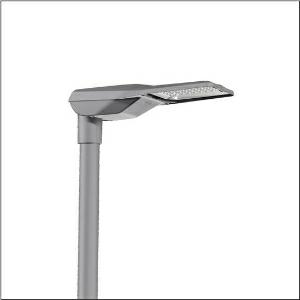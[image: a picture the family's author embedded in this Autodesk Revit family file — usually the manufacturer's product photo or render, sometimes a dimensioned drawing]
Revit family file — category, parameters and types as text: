
# Revit family: streetlight_sl_21_iq_mini___st0_8a_5xe2c31d08hb_f94e
name_source: partatom
category: Lighting Fixtures
units: mm (PartAtom-declared; Revit-internal decimal feet)

## family parameters
Cut with Voids When Loaded = No
Host = Face
Light Source = No
Part Type = Normal
Room Calculation Point = No
Round Connector Dimension = Use Diameter
Shared = No

## types (1)
- --- (1 x LED, 9450 lm, 70.9 W, 3000K)
    Apparent Load = 71 VA
    CIE Flux Codes = 38 75 97 100 100
    Color Rendering = 70
    Color Temperature = 3000K
    Default Elevation = 1800 mm
    Description = Streetlight SL 21 iQ mini, mast luminaire, primary light control with lens, of PMMA, primary optical cover: cover, of toughened safety glass, transparent, light distribution: ST0.8a, light emission: direct distribution, primary light characteristic: asymmetric, installation type: post-top, side-entry, LED, High Power LED, rated luminous flux: 9.450lm, luminous efficacy: 133lm/W, light colour: 730, colour temperature: 3000K, control gear: iQ-Comfort, control: Auto-Match, Temp-Guard, Lumen-Switch, Night-Set, Smart-Wire, Light-Fading, Desk-Remote (wireless, voltage-free reading and setting of iQ features in the workshop via application-optimized NFC function/RFID function), optimised constant luminous flux control (CLO 2.0), pre-setting: linear dimming characteristic, mains connection: 220..240V, AC, 50/60Hz, start of lifetime: 71W, end of service life: 75W, reduction: 31W, luminaire housing, of diecast aluminium, powder-coated, Siteco® metallic grey (DB 702S), corrosivity category C5 mid according to DIN EN ISO 12944, please order mast flange separately, inclination adjustable: 0°, 5°, 10°, 15°, sealing non-destructively replaceable, multi-level sealing system, length: 628mm, width: 235mm, height: 110mm, mast flange for spigot size: 42mm (side-entry): 5XC10008XM4, 60/48mm (side-entry/post-top): 5XC10108XM2, 76/60mm (side-entry/post-top): 5XC10108XM1, mounting height: 4..8m, protection rating (complete): IP66, insulation class (complete): insulation class II (safety insulation), certification: CE, ENEC, ENEC+, VDE, impact resistance: IK10, permissible operating ambient temperature for outdoor applications: -40..+50°C, standard-compliant lighting for roads and squares, packaging unit: 1 piece

Light Distribution: ST0.8a
    Height = 110 mm
    Lamp = 1 x LED
    Lamp Light Flux = 9450 lm
    Lamp Power = 70.9 W
    Lamp count = 1
    Length = 625 mm
    Luminous efficacy = 133 lm/W
    Manufacturer = Siteco
    ModVariant = No
    Model = 5XE2C31D08HB
    Number of Poles = 1
    OnlyDefault = Yes
    Power Factor = 1
    Product Name = Streetlight SL 21 iQ mini | ST0.8a
    Product group = mast luminaire | pylon top
    ProductGroupID = 6100
    Protection Class = Protection class II
    Protection Degree = IP 66
    RLX_Detail_Level = 1
    RLX_Emergency_Light_Flux = 0 lm
    RLX_Emergency_Type = 0
    RLX_Emergency_Type_DB = No
    RlxData = <blob elided: 26409 chars, md5=41995c7d>
    Socket = socket
    Standby Power = 0 W
    System Light Flux = 9450 lm
    System Power = 71 W
    Type Comments = factory setting: luminous flux: 100 % | dim-lin: 254 | 711 mA
    Type Image = l_1003519.jpg
    URL = http://relux.com
    VarID = @adj_157466
    Voltage = 0 V
    Weight = 0.00 kg
    Width = 234 mm

## geometry (parser evidence)
native form markers: Blend x4, Sweep x12
no freeform markers — native parametric forms only
